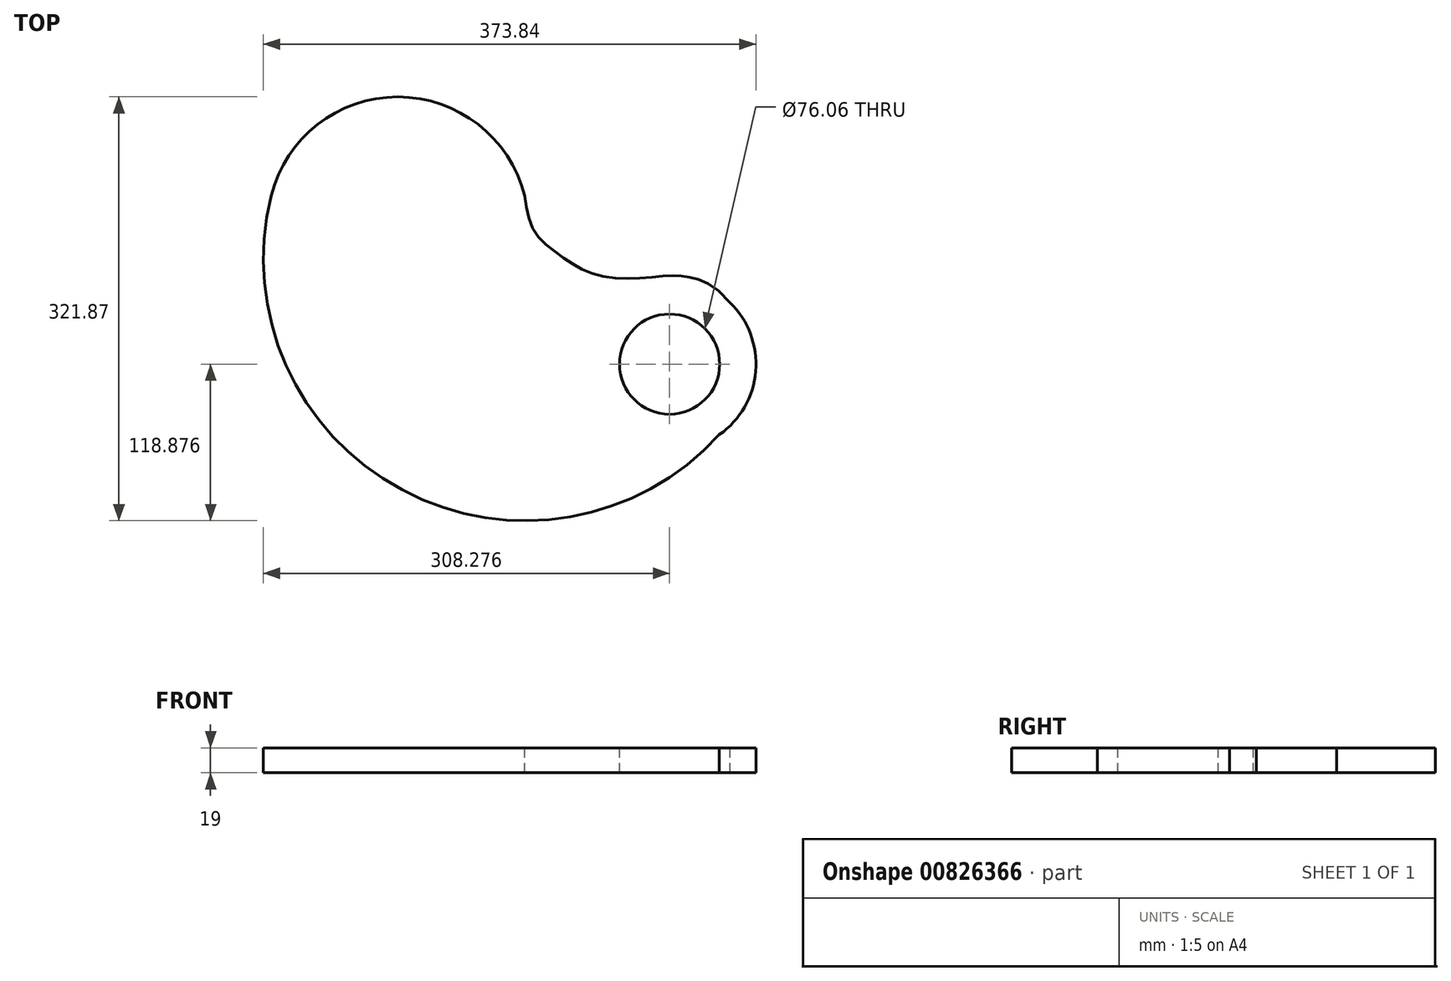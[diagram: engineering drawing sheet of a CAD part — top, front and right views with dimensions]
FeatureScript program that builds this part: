
annotation { "Feature Type Name" : "Feature", "Feature Type Description" : "" }
export const myFeature = defineFeature(function(context is Context, id is Id, definition is map)
    precondition{}
    {
        {
            var Q0;
            Q0=qCreatedBy(makeId("Top.planeOp"),FACE);
            var sketch = newSketch(context, id + "F0", { "sketchPlane" : qUnion([Q0])});
            skLineSegment(sketch, "E0.bottom", {"start": v(200, 175) * mm, "end": v(-200, 175) * mm});
            skLineSegment(sketch, "E0.top", {"start": v(200, -175) * mm, "end": v(-200, -175) * mm});
            skLineSegment(sketch, "E0.left", {"start": v(200, 175) * mm, "end": v(200, -175) * mm});
            skLineSegment(sketch, "E0.right", {"start": v(-200, 175) * mm, "end": v(-200, -175) * mm});
            skPoint(sketch, "E0.middle", {"position": v(0, 0) * mm});
            skSolve(sketch);
        }
        {
            var Q0;
            Q0=makeQuery(id+"F0.imprint","IMPRINT",FACE,{"disambiguationData":[TD([[makeQuery(id+"F0.imprint","IMPRINT",EDGE,{"derivedFrom":sQuery(id+"F0.wireOp",EDGE,"E0.bottom")}),1.0]])]});
            extrude(context, id + "F1", {"entities" : qUnion([Q0]), "depth" : 19 * mm, "offsetDistance" : 25 * mm});
        }
        {
            var Q0;
            Q0=makeQuery(id+"F1.opExtrude","CAP_FACE",FACE,{"disambiguationData":[OSD([sQuery(id+"F0.wireOp",EDGE,"E0.bottom"),sQuery(id+"F0.wireOp",EDGE,"E0.top"),sQuery(id+"F0.wireOp",EDGE,"E0.left"),sQuery(id+"F0.wireOp",EDGE,"E0.right")])],"isStart":false});
            var sketch = newSketch(context, id + "F2", { "sketchPlane" : qUnion([Q0])});
            skArc(sketch, "E1", {"start": v(-181.72, 81.27) * mm, "mid": v(-82.45, -142.2) * mm, "end": v(158.47, -100.3) * mm});
            skArc(sketch, "E2", {"start": v(10.6, 81.27) * mm, "mid": v(-85.56, 156.25) * mm, "end": v(-181.72, 81.27) * mm});
            skArc(sketch, "E3", {"start": v(158.47, -100.3) * mm, "mid": v(186, -52.06) * mm, "end": v(166.63, 0) * mm});
            skFitSpline(sketch, "E4", {"points": [v(10.6, 81.27) * mm, v(18.21, 54.1) * mm, v(37.24, 36.15) * mm, v(60.62, 22.56) * mm, v(92.15, 18.21) * mm, v(121.5, 20.39) * mm, v(137.81, 18.76) * mm, v(166.63, 0) * mm], "startDerivative": vector(30.03, -196.02) * mm, "endDerivative": vector(213.82, -259.64) * mm});
            skCircle(sketch, "E5", {"center": v(120.65, -46.74) * mm, "radius": 31.62 * mm});
            skSolve(sketch);
        }
        {
            var Q0;
            Q0=makeQuery(id+"F2.imprint","IMPRINT",FACE,{"disambiguationData":[TD([[makeQuery(id+"F2.imprint","IMPRINT",EDGE,{"derivedFrom":sQuery(id+"F2.wireOp",EDGE,"E1")}),-1.0]])]});
            extrude(context, id + "F3", {"entities" : qUnion([Q0]), "operationType" : NewBodyOperationType.REMOVE, "endBound" : BoundingType.THROUGH_ALL, "oppositeDirection" : true, "depth" : 25 * mm, "offsetDistance" : 25 * mm});
        }
        {
            var Q0;
            Q0=makeQuery(id+"F1.opExtrude","CAP_FACE",FACE,{"disambiguationData":[OSD([sQuery(id+"F0.wireOp",EDGE,"E0.bottom"),sQuery(id+"F0.wireOp",EDGE,"E0.top"),sQuery(id+"F0.wireOp",EDGE,"E0.left"),sQuery(id+"F0.wireOp",EDGE,"E0.right")])],"isStart":false});
            var sketch = newSketch(context, id + "F4", { "sketchPlane" : qUnion([Q0])});
            skCircle(sketch, "E6", {"center": v(120.65, -46.74) * mm, "radius": 38.03 * mm});
            skSolve(sketch);
        }
        {
            var Q0;
            Q0=makeQuery(id+"F4.imprint","IMPRINT",FACE,{"disambiguationData":[TD([[makeQuery(id+"F4.imprint","IMPRINT",EDGE,{"derivedFrom":sQuery(id+"F4.wireOp",EDGE,"E6")}),1.0]])]});
            extrude(context, id + "F5", {"entities" : qUnion([Q0]), "operationType" : NewBodyOperationType.REMOVE, "endBound" : BoundingType.THROUGH_ALL, "oppositeDirection" : true, "depth" : 25 * mm, "offsetDistance" : 25 * mm});
        }
    });
